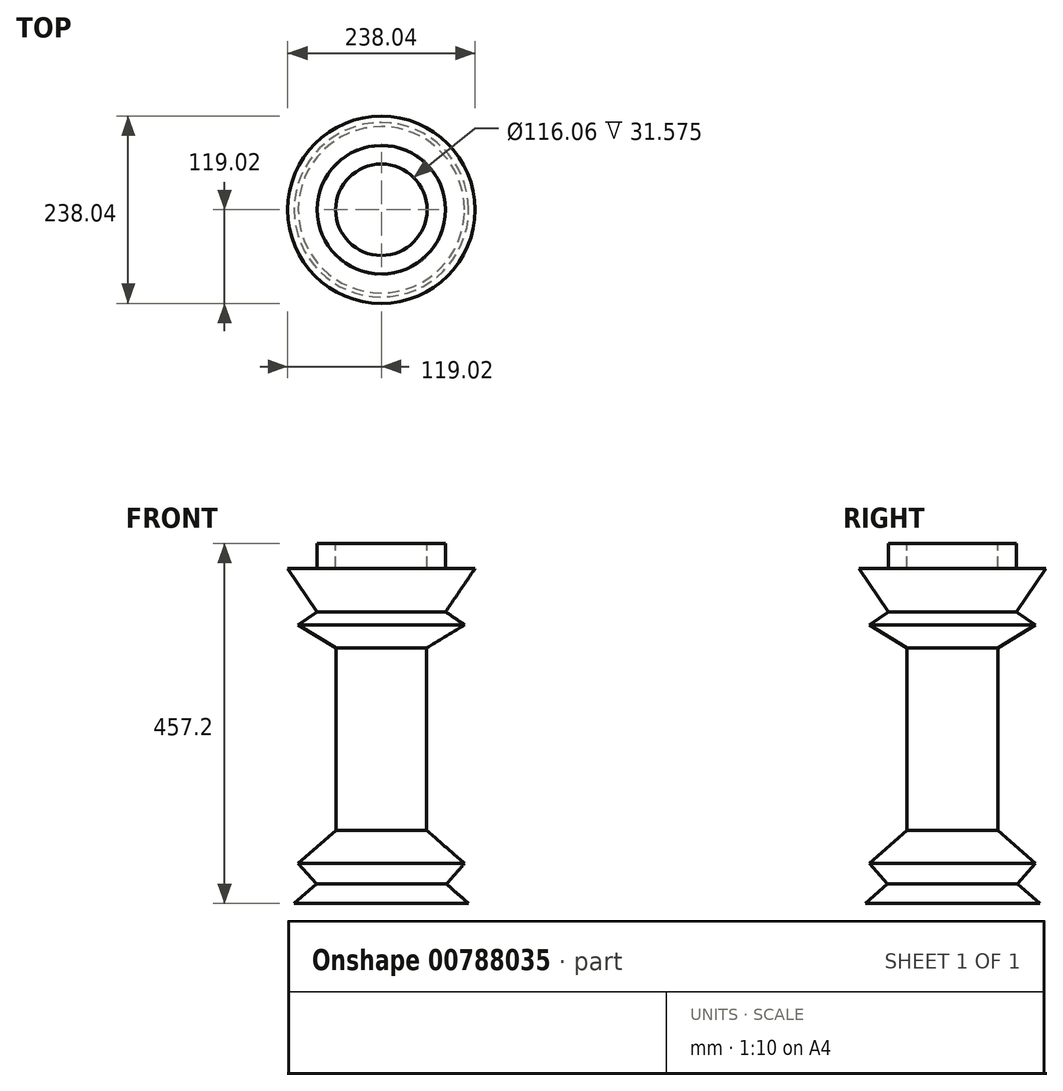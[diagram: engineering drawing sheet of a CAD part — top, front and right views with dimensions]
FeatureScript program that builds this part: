
annotation { "Feature Type Name" : "Feature", "Feature Type Description" : "" }
export const myFeature = defineFeature(function(context is Context, id is Id, definition is map)
    precondition{}
    {
        {
            var Q0;
            Q0=qCreatedBy(makeId("Front.planeOp"),FACE);
            var sketch = newSketch(context, id + "F0", { "sketchPlane" : qUnion([Q0])});
            skLineSegment(sketch, "E0", {"start": v(0, 339.38) * mm, "end": v(0, -342.9) * mm});
            skLineSegment(sketch, "E1", {"start": v(0, -342.9) * mm, "end": v(-110.78, -342.9) * mm});
            skLineSegment(sketch, "E2", {"start": v(-110.78, -342.9) * mm, "end": v(-82.65, -318.28) * mm});
            skLineSegment(sketch, "E3", {"start": v(-82.65, -318.28) * mm, "end": v(-105.6, -292.06) * mm});
            skLineSegment(sketch, "E4", {"start": v(-105.6, -292.06) * mm, "end": v(-57.54, -250) * mm});
            skLineSegment(sketch, "E5", {"start": v(-57.54, -250) * mm, "end": v(-57.54, -18.17) * mm});
            skLineSegment(sketch, "E6", {"start": v(-57.54, -18.17) * mm, "end": v(-105.6, 11.14) * mm});
            skLineSegment(sketch, "E7", {"start": v(-105.6, 11.14) * mm, "end": v(-81.48, 27.55) * mm});
            skLineSegment(sketch, "E8", {"start": v(-81.48, 27.55) * mm, "end": v(-119.02, 82.72) * mm});
            skLineSegment(sketch, "E9", {"start": v(-119.02, 82.72) * mm, "end": v(0, 82.72) * mm});
            skLineSegment(sketch, "E10", {"start": v(-81.57, 82.72) * mm, "end": v(-81.57, 114.3) * mm});
            skPoint(sketch, "E10.startSnap0", {"position": v(-81.57, -3.52) * mm});
            skLineSegment(sketch, "E11", {"start": v(-81.57, 114.3) * mm, "end": v(-58.03, 114.3) * mm});
            skLineSegment(sketch, "E12", {"start": v(-58.03, 114.3) * mm, "end": v(-58.03, 82.72) * mm});
            skSolve(sketch);
        }
        {
            var Q0;
            Q0=qSketchRegion(id+"F0",true);
            var Q1;
            Q1=sQuery(id+"F0.wireOp",EDGE,"E0");
            revolve(context, id + "F1", {"surfaceOperationType" : NewSurfaceOperationType.NEW, "entities" : qUnion([Q0]), "axis" : qUnion([Q1]), "revolveType" : RevolveType.FULL});
        }
    });
